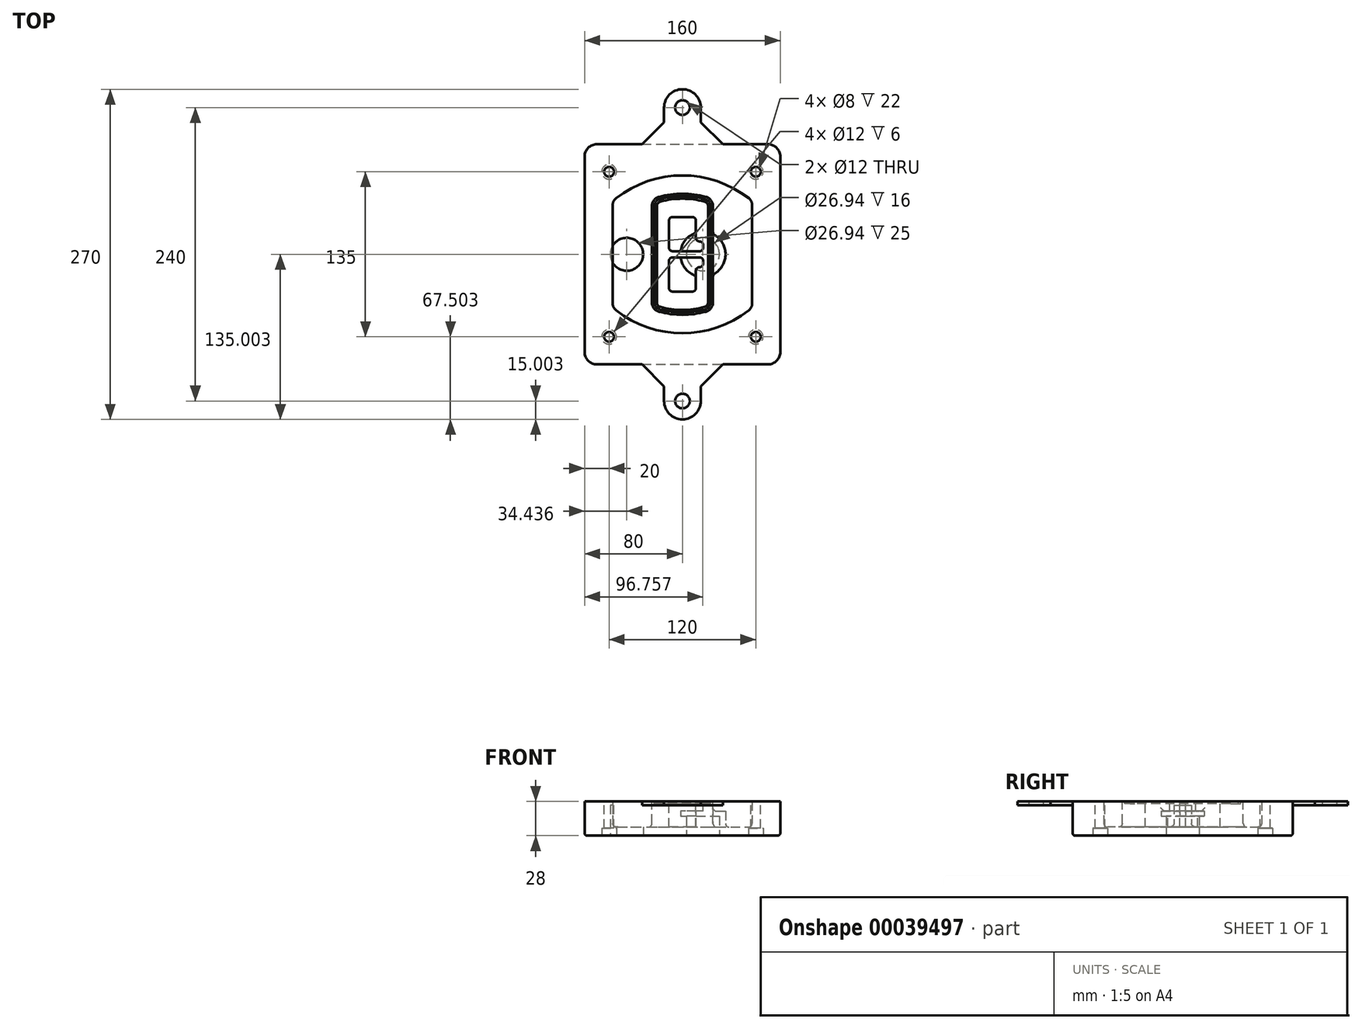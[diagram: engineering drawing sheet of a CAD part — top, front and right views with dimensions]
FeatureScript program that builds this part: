
annotation { "Feature Type Name" : "Feature", "Feature Type Description" : "" }
export const myFeature = defineFeature(function(context is Context, id is Id, definition is map)
    precondition{}
    {
        {
            var Q0;
            Q0=qCreatedBy(makeId("Top.planeOp"),FACE);
            var sketch = newSketch(context, id + "F0", { "sketchPlane" : qUnion([Q0])});
            skPoint(sketch, "E0.rect.middle", {"position": v(0, 0) * mm});
            skLineSegment(sketch, "E1.bottom", {"start": v(24.05, 28.38) * mm, "end": v(164.05, 28.38) * mm});
            skLineSegment(sketch, "E1.top", {"start": v(24.05, 208.38) * mm, "end": v(164.05, 208.38) * mm});
            skLineSegment(sketch, "E1.left", {"start": v(14.05, 38.38) * mm, "end": v(14.05, 198.38) * mm});
            skLineSegment(sketch, "E1.right", {"start": v(174.05, 38.38) * mm, "end": v(174.05, 198.38) * mm});
            skLineSegment(sketch, "E2", {"start": v(14.05, 208.38) * mm, "end": v(174.05, 28.38) * mm, "construction": true});
            skLineSegment(sketch, "E3", {"start": v(174.05, 208.38) * mm, "end": v(14.05, 28.38) * mm, "construction": true});
            skCircle(sketch, "E4", {"center": v(34.05, 185.88) * mm, "radius": 4 * mm});
            skCircle(sketch, "E5", {"center": v(154.05, 185.88) * mm, "radius": 4 * mm});
            skCircle(sketch, "E6", {"center": v(154.05, 50.88) * mm, "radius": 4 * mm});
            skCircle(sketch, "E7", {"center": v(34.05, 50.88) * mm, "radius": 4 * mm});
            skLineSegment(sketch, "E8", {"start": v(34.05, 185.88) * mm, "end": v(154.05, 185.88) * mm, "construction": true});
            skLineSegment(sketch, "E9", {"start": v(154.05, 185.88) * mm, "end": v(154.05, 50.88) * mm, "construction": true});
            skLineSegment(sketch, "E10", {"start": v(154.05, 50.88) * mm, "end": v(34.05, 50.88) * mm, "construction": true});
            skLineSegment(sketch, "E11", {"start": v(34.05, 50.88) * mm, "end": v(34.05, 185.88) * mm, "construction": true});
            skLineSegment(sketch, "E12", {"start": v(34.05, 158.68) * mm, "end": v(34.05, 78.09) * mm});
            skLineSegment(sketch, "E13", {"start": v(154.05, 158.68) * mm, "end": v(154.05, 78.09) * mm});
            skArc(sketch, "E14", {"start": v(150.2, 166.56) * mm, "mid": v(94.05, 185.88) * mm, "end": v(37.9, 166.56) * mm});
            skArc(sketch, "E15", {"start": v(37.9, 70.2) * mm, "mid": v(94.05, 50.88) * mm, "end": v(150.2, 70.2) * mm});
            skLineSegment(sketch, "E16", {"start": v(34.05, 118.38) * mm, "end": v(154.05, 118.38) * mm, "construction": true});
            skPoint(sketch, "E17.visualSharp", {"position": v(34.05, 73.38) * mm});
            skArc(sketch, "E17.filletArc", {"start": v(34.05, 78.09) * mm, "mid": v(35.06, 73.7) * mm, "end": v(37.9, 70.2) * mm});
            skPoint(sketch, "E18.visualSharp", {"position": v(34.05, 163.38) * mm});
            skArc(sketch, "E18.filletArc", {"start": v(37.9, 166.56) * mm, "mid": v(35.06, 163.06) * mm, "end": v(34.05, 158.68) * mm});
            skPoint(sketch, "E19.visualSharp", {"position": v(154.05, 163.38) * mm});
            skArc(sketch, "E19.filletArc", {"start": v(154.05, 158.68) * mm, "mid": v(153.04, 163.06) * mm, "end": v(150.2, 166.56) * mm});
            skPoint(sketch, "E20.visualSharp", {"position": v(154.05, 73.38) * mm});
            skArc(sketch, "E20.filletArc", {"start": v(150.2, 70.2) * mm, "mid": v(153.04, 73.7) * mm, "end": v(154.05, 78.09) * mm});
            skPoint(sketch, "E21.visualSharp", {"position": v(14.05, 208.38) * mm});
            skArc(sketch, "E21.filletArc", {"start": v(24.05, 208.38) * mm, "mid": v(16.98, 205.45) * mm, "end": v(14.05, 198.38) * mm});
            skPoint(sketch, "E22.visualSharp", {"position": v(174.05, 208.38) * mm});
            skArc(sketch, "E22.filletArc", {"start": v(174.05, 198.38) * mm, "mid": v(171.12, 205.45) * mm, "end": v(164.05, 208.38) * mm});
            skPoint(sketch, "E23.visualSharp", {"position": v(174.05, 28.38) * mm});
            skArc(sketch, "E23.filletArc", {"start": v(164.05, 28.38) * mm, "mid": v(171.12, 31.31) * mm, "end": v(174.05, 38.38) * mm});
            skPoint(sketch, "E24.visualSharp", {"position": v(14.05, 28.38) * mm});
            skArc(sketch, "E24.filletArc", {"start": v(14.05, 38.38) * mm, "mid": v(16.98, 31.31) * mm, "end": v(24.05, 28.38) * mm});
            skArc(sketch, "E25.0", {"start": v(151.05, 158.68) * mm, "mid": v(150.34, 161.75) * mm, "end": v(148.36, 164.2) * mm});
            skLineSegment(sketch, "E25.1", {"start": v(151.05, 158.68) * mm, "end": v(151.05, 78.09) * mm});
            skArc(sketch, "E25.2", {"start": v(148.36, 72.57) * mm, "mid": v(150.34, 75.02) * mm, "end": v(151.05, 78.09) * mm});
            skArc(sketch, "E25.3", {"start": v(39.74, 72.57) * mm, "mid": v(94.05, 53.88) * mm, "end": v(148.36, 72.57) * mm});
            skArc(sketch, "E25.4", {"start": v(37.05, 78.09) * mm, "mid": v(37.76, 75.02) * mm, "end": v(39.74, 72.57) * mm});
            skArc(sketch, "E25.5", {"start": v(148.36, 164.2) * mm, "mid": v(94.05, 182.88) * mm, "end": v(39.74, 164.2) * mm});
            skLineSegment(sketch, "E25.6", {"start": v(37.05, 158.68) * mm, "end": v(37.05, 78.09) * mm});
            skArc(sketch, "E25.7", {"start": v(39.74, 164.2) * mm, "mid": v(37.76, 161.75) * mm, "end": v(37.05, 158.68) * mm});
            skArc(sketch, "E26.0", {"start": v(35.43, 169.71) * mm, "mid": v(31.47, 164.82) * mm, "end": v(30.05, 158.68) * mm});
            skArc(sketch, "E26.1", {"start": v(152.67, 169.71) * mm, "mid": v(94.05, 189.88) * mm, "end": v(35.43, 169.71) * mm});
            skArc(sketch, "E26.2", {"start": v(158.05, 158.68) * mm, "mid": v(156.63, 164.82) * mm, "end": v(152.67, 169.71) * mm});
            skLineSegment(sketch, "E26.3", {"start": v(158.05, 158.68) * mm, "end": v(158.05, 78.09) * mm});
            skArc(sketch, "E26.4", {"start": v(152.67, 67.05) * mm, "mid": v(156.63, 71.95) * mm, "end": v(158.05, 78.09) * mm});
            skLineSegment(sketch, "E26.5", {"start": v(30.05, 158.68) * mm, "end": v(30.05, 78.09) * mm});
            skArc(sketch, "E26.6", {"start": v(35.43, 67.05) * mm, "mid": v(94.05, 46.88) * mm, "end": v(152.67, 67.05) * mm});
            skArc(sketch, "E26.7", {"start": v(30.05, 78.09) * mm, "mid": v(31.47, 71.95) * mm, "end": v(35.43, 67.05) * mm});
            skSolve(sketch);
        }
        {
            var Q0;
            Q0=makeQuery(id+"F0.imprint","IMPRINT",FACE,{"disambiguationData":[TD([[makeQuery(id+"F0.imprint","IMPRINT",EDGE,{"derivedFrom":sQuery(id+"F0.wireOp",EDGE,"E1.bottom")}),1.0]])]});
            var Q1;
            Q1=makeQuery(id+"F0.imprint","IMPRINT",FACE,{"disambiguationData":[TD([[makeQuery(id+"F0.imprint","IMPRINT",EDGE,{"derivedFrom":sQuery(id+"F0.wireOp",EDGE,"E12")}),1.0]])]});
            var Q2;
            Q2=makeQuery(id+"F0.imprint","IMPRINT",FACE,{"disambiguationData":[TD([[makeQuery(id+"F0.imprint","IMPRINT",EDGE,{"derivedFrom":sQuery(id+"F0.wireOp",EDGE,"E25.0")}),1.0]])]});
            var Q3;
            Q3=makeQuery(id+"F0.imprint","IMPRINT",FACE,{"disambiguationData":[TD([[makeQuery(id+"F0.imprint","IMPRINT",EDGE,{"derivedFrom":sQuery(id+"F0.wireOp",EDGE,"E12")}),-1.0]])]});
            extrude(context, id + "F1", {"entities" : qUnion([Q0, Q1, Q2, Q3]), "oppositeDirection" : true, "depth" : 25 * mm});
        }
        {
            var Q0;
            Q0=makeQuery(id+"F0.imprint","IMPRINT",FACE,{"disambiguationData":[TD([[makeQuery(id+"F0.imprint","IMPRINT",EDGE,{"derivedFrom":sQuery(id+"F0.wireOp",EDGE,"E12")}),1.0]])]});
            extrude(context, id + "F2", {"entities" : qUnion([Q0]), "operationType" : NewBodyOperationType.ADD, "depth" : 3 * mm});
        }
        {
            var Q0;
            Q0=makeQuery(id+"F0.imprint","IMPRINT",FACE,{"disambiguationData":[TD([[makeQuery(id+"F0.imprint","IMPRINT",EDGE,{"derivedFrom":sQuery(id+"F0.wireOp",EDGE,"E25.0")}),1.0]])]});
            extrude(context, id + "F3", {"entities" : qUnion([Q0]), "operationType" : NewBodyOperationType.REMOVE, "oppositeDirection" : true, "depth" : 18 * mm});
        }
        {
            var Q0;
            Q0=makeQuery(id+"F2.opExtrude","CAP_FACE",FACE,{"disambiguationData":[OSD([sQuery(id+"F0.wireOp",EDGE,"E12"),sQuery(id+"F0.wireOp",EDGE,"E13"),sQuery(id+"F0.wireOp",EDGE,"E14"),sQuery(id+"F0.wireOp",EDGE,"E15"),sQuery(id+"F0.wireOp",EDGE,"E17.filletArc"),sQuery(id+"F0.wireOp",EDGE,"E18.filletArc"),sQuery(id+"F0.wireOp",EDGE,"E19.filletArc"),sQuery(id+"F0.wireOp",EDGE,"E20.filletArc"),sQuery(id+"F0.wireOp",EDGE,"E25.0"),sQuery(id+"F0.wireOp",EDGE,"E25.1"),sQuery(id+"F0.wireOp",EDGE,"E25.2"),sQuery(id+"F0.wireOp",EDGE,"E25.3"),sQuery(id+"F0.wireOp",EDGE,"E25.4"),sQuery(id+"F0.wireOp",EDGE,"E25.5"),sQuery(id+"F0.wireOp",EDGE,"E25.6"),sQuery(id+"F0.wireOp",EDGE,"E25.7")])],"isStart":false});
            var sketch = newSketch(context, id + "F4", { "sketchPlane" : qUnion([Q0])});
            skArc(sketch, "E27.0", {"start": v(74.97, 71.41) * mm, "mid": v(94.05, 68.88) * mm, "end": v(113.13, 71.41) * mm});
            skArc(sketch, "E28.0", {"start": v(113.13, 165.35) * mm, "mid": v(94.05, 167.88) * mm, "end": v(74.97, 165.35) * mm});
            skLineSegment(sketch, "E29", {"start": v(69.05, 157.63) * mm, "end": v(69.05, 79.14) * mm});
            skLineSegment(sketch, "E30", {"start": v(119.05, 157.63) * mm, "end": v(119.05, 79.14) * mm});
            skLineSegment(sketch, "E31", {"start": v(69.05, 163.48) * mm, "end": v(119.05, 163.48) * mm, "construction": true});
            skLineSegment(sketch, "E32", {"start": v(69.05, 73.28) * mm, "end": v(119.05, 73.28) * mm, "construction": true});
            skPoint(sketch, "E33.visualSharp", {"position": v(69.05, 163.48) * mm});
            skArc(sketch, "E33.filletArc", {"start": v(74.97, 165.35) * mm, "mid": v(70.7, 162.5) * mm, "end": v(69.05, 157.63) * mm});
            skPoint(sketch, "E34.visualSharp", {"position": v(119.05, 163.48) * mm});
            skArc(sketch, "E34.filletArc", {"start": v(119.05, 157.63) * mm, "mid": v(117.4, 162.5) * mm, "end": v(113.13, 165.35) * mm});
            skPoint(sketch, "E35.visualSharp", {"position": v(119.05, 73.28) * mm});
            skArc(sketch, "E35.filletArc", {"start": v(113.13, 71.41) * mm, "mid": v(117.4, 74.27) * mm, "end": v(119.05, 79.14) * mm});
            skPoint(sketch, "E36.visualSharp", {"position": v(69.05, 73.28) * mm});
            skArc(sketch, "E36.filletArc", {"start": v(69.05, 79.14) * mm, "mid": v(70.7, 74.27) * mm, "end": v(74.97, 71.41) * mm});
            skArc(sketch, "E37.0", {"start": v(148.36, 164.2) * mm, "mid": v(94.05, 182.88) * mm, "end": v(39.74, 164.2) * mm});
            skArc(sketch, "E37.1", {"start": v(39.74, 164.2) * mm, "mid": v(37.76, 161.75) * mm, "end": v(37.05, 158.68) * mm});
            skLineSegment(sketch, "E37.2", {"start": v(37.05, 158.68) * mm, "end": v(37.05, 78.09) * mm});
            skArc(sketch, "E37.3", {"start": v(37.05, 78.09) * mm, "mid": v(37.76, 75.02) * mm, "end": v(39.74, 72.57) * mm});
            skArc(sketch, "E37.4", {"start": v(39.74, 72.57) * mm, "mid": v(94.05, 53.88) * mm, "end": v(148.36, 72.57) * mm});
            skArc(sketch, "E37.5", {"start": v(148.36, 72.57) * mm, "mid": v(150.34, 75.02) * mm, "end": v(151.05, 78.09) * mm});
            skLineSegment(sketch, "E37.6", {"start": v(151.05, 158.68) * mm, "end": v(151.05, 78.09) * mm});
            skArc(sketch, "E37.7", {"start": v(151.05, 158.68) * mm, "mid": v(150.34, 161.75) * mm, "end": v(148.36, 164.2) * mm});
            skLineSegment(sketch, "E38.0", {"start": v(117.05, 157.63) * mm, "end": v(117.05, 79.14) * mm});
            skArc(sketch, "E38.1", {"start": v(112.61, 73.34) * mm, "mid": v(115.81, 75.49) * mm, "end": v(117.05, 79.14) * mm});
            skArc(sketch, "E38.2", {"start": v(75.49, 73.34) * mm, "mid": v(94.05, 70.88) * mm, "end": v(112.61, 73.34) * mm});
            skArc(sketch, "E38.3", {"start": v(71.05, 79.14) * mm, "mid": v(72.29, 75.49) * mm, "end": v(75.49, 73.34) * mm});
            skLineSegment(sketch, "E38.4", {"start": v(71.05, 157.63) * mm, "end": v(71.05, 79.14) * mm});
            skArc(sketch, "E38.5", {"start": v(117.05, 157.63) * mm, "mid": v(115.81, 161.28) * mm, "end": v(112.61, 163.42) * mm});
            skArc(sketch, "E38.6", {"start": v(75.49, 163.42) * mm, "mid": v(72.29, 161.28) * mm, "end": v(71.05, 157.63) * mm});
            skArc(sketch, "E38.7", {"start": v(112.61, 163.42) * mm, "mid": v(94.05, 165.88) * mm, "end": v(75.49, 163.42) * mm});
            skArc(sketch, "E39.0", {"start": v(115.05, 157.63) * mm, "mid": v(114.23, 160.06) * mm, "end": v(112.1, 161.5) * mm});
            skLineSegment(sketch, "E39.1", {"start": v(115.05, 157.63) * mm, "end": v(115.05, 79.14) * mm});
            skArc(sketch, "E39.2", {"start": v(112.1, 75.27) * mm, "mid": v(114.23, 76.7) * mm, "end": v(115.05, 79.14) * mm});
            skArc(sketch, "E39.3", {"start": v(76, 75.27) * mm, "mid": v(94.05, 72.88) * mm, "end": v(112.1, 75.27) * mm});
            skArc(sketch, "E39.4", {"start": v(73.05, 79.14) * mm, "mid": v(73.87, 76.7) * mm, "end": v(76, 75.27) * mm});
            skArc(sketch, "E39.5", {"start": v(112.1, 161.5) * mm, "mid": v(94.05, 163.88) * mm, "end": v(76, 161.5) * mm});
            skLineSegment(sketch, "E39.6", {"start": v(73.05, 157.63) * mm, "end": v(73.05, 79.14) * mm});
            skArc(sketch, "E39.7", {"start": v(76, 161.5) * mm, "mid": v(73.87, 160.06) * mm, "end": v(73.05, 157.63) * mm});
            skLineSegment(sketch, "E40", {"start": v(69.05, 118.38) * mm, "end": v(119.05, 118.38) * mm, "construction": true});
            skLineSegment(sketch, "E41", {"start": v(83.05, 123.88) * mm, "end": v(83.05, 145.88) * mm});
            skLineSegment(sketch, "E42", {"start": v(86.05, 148.88) * mm, "end": v(102.05, 148.88) * mm});
            skLineSegment(sketch, "E43", {"start": v(105.05, 145.88) * mm, "end": v(105.05, 131.88) * mm});
            skLineSegment(sketch, "E44", {"start": v(108.05, 128.88) * mm, "end": v(108.05, 128.88) * mm});
            skLineSegment(sketch, "E45", {"start": v(111.05, 125.88) * mm, "end": v(111.05, 123.88) * mm});
            skLineSegment(sketch, "E46", {"start": v(108.05, 120.88) * mm, "end": v(86.05, 120.88) * mm});
            skPoint(sketch, "E47.visualSharp", {"position": v(83.05, 148.88) * mm});
            skArc(sketch, "E47.filletArc", {"start": v(86.05, 148.88) * mm, "mid": v(83.93, 148) * mm, "end": v(83.05, 145.88) * mm});
            skPoint(sketch, "E48.visualSharp", {"position": v(105.05, 148.88) * mm});
            skArc(sketch, "E48.filletArc", {"start": v(105.05, 145.88) * mm, "mid": v(104.17, 148) * mm, "end": v(102.05, 148.88) * mm});
            skPoint(sketch, "E49.visualSharp", {"position": v(105.05, 128.88) * mm});
            skArc(sketch, "E49.filletArc", {"start": v(105.05, 131.88) * mm, "mid": v(105.93, 129.76) * mm, "end": v(108.05, 128.88) * mm});
            skPoint(sketch, "E50.visualSharp", {"position": v(111.05, 128.88) * mm});
            skArc(sketch, "E50.filletArc", {"start": v(111.05, 125.88) * mm, "mid": v(110.17, 128) * mm, "end": v(108.05, 128.88) * mm});
            skPoint(sketch, "E51.visualSharp", {"position": v(111.05, 120.88) * mm});
            skArc(sketch, "E51.filletArc", {"start": v(108.05, 120.88) * mm, "mid": v(110.17, 121.76) * mm, "end": v(111.05, 123.88) * mm});
            skPoint(sketch, "E52.visualSharp", {"position": v(83.05, 120.88) * mm});
            skArc(sketch, "E52.filletArc", {"start": v(83.05, 123.88) * mm, "mid": v(83.93, 121.76) * mm, "end": v(86.05, 120.88) * mm});
            skLineSegment(sketch, "E53.0.MirrorCS", {"start": v(108.05, 115.88) * mm, "end": v(86.05, 115.88) * mm});
            skArc(sketch, "E54.0.MirrorCS", {"start": v(83.05, 112.88) * mm, "mid": v(83.93, 115) * mm, "end": v(86.05, 115.88) * mm});
            skLineSegment(sketch, "E55.0.MirrorCS", {"start": v(83.05, 112.88) * mm, "end": v(83.05, 90.88) * mm});
            skArc(sketch, "E56.0.MirrorCS", {"start": v(86.05, 87.88) * mm, "mid": v(83.93, 88.76) * mm, "end": v(83.05, 90.88) * mm});
            skLineSegment(sketch, "E57.0.MirrorCS", {"start": v(86.05, 87.88) * mm, "end": v(102.05, 87.88) * mm});
            skArc(sketch, "E58.0.MirrorCS", {"start": v(105.05, 90.88) * mm, "mid": v(104.17, 88.76) * mm, "end": v(102.05, 87.88) * mm});
            skLineSegment(sketch, "E59.0.MirrorCS", {"start": v(105.05, 90.88) * mm, "end": v(105.05, 104.88) * mm});
            skArc(sketch, "E60.0.MirrorCS", {"start": v(105.05, 104.88) * mm, "mid": v(105.93, 107) * mm, "end": v(108.05, 107.88) * mm});
            skArc(sketch, "E61.0.MirrorCS", {"start": v(111.05, 110.88) * mm, "mid": v(110.17, 108.76) * mm, "end": v(108.05, 107.88) * mm});
            skLineSegment(sketch, "E62.0.MirrorCS", {"start": v(111.05, 110.88) * mm, "end": v(111.05, 112.88) * mm});
            skArc(sketch, "E63.0.MirrorCS", {"start": v(108.05, 115.88) * mm, "mid": v(110.17, 115) * mm, "end": v(111.05, 112.88) * mm});
            skSolve(sketch);
        }
        {
            var Q0;
            Q0=makeQuery(id+"F4.imprint","IMPRINT",FACE,{"disambiguationData":[TD([[makeQuery(id+"F4.imprint","IMPRINT",EDGE,{"derivedFrom":sQuery(id+"F4.wireOp",EDGE,"E27.0")}),1.0]])]});
            var Q1;
            Q1=makeQuery(id+"F4.imprint","IMPRINT",FACE,{"disambiguationData":[TD([[makeQuery(id+"F4.imprint","IMPRINT",EDGE,{"derivedFrom":sQuery(id+"F4.wireOp",EDGE,"E38.0")}),-1.0]])]});
            var Q2;
            Q2=makeQuery(id+"F4.imprint","IMPRINT",FACE,{"disambiguationData":[TD([[makeQuery(id+"F4.imprint","IMPRINT",EDGE,{"derivedFrom":sQuery(id+"F4.wireOp",EDGE,"E39.0")}),1.0]])]});
            extrude(context, id + "F5", {"entities" : qUnion([Q0, Q1, Q2]), "operationType" : NewBodyOperationType.ADD, "endBound" : BoundingType.UP_TO_NEXT, "oppositeDirection" : true, "depth" : 25 * mm});
        }
        {
            var Q0;
            Q0=makeQuery(id+"F4.imprint","IMPRINT",FACE,{"disambiguationData":[TD([[makeQuery(id+"F4.imprint","IMPRINT",EDGE,{"derivedFrom":sQuery(id+"F4.wireOp",EDGE,"E38.0")}),-1.0]])]});
            extrude(context, id + "F6", {"entities" : qUnion([Q0]), "operationType" : NewBodyOperationType.REMOVE, "oppositeDirection" : true, "depth" : 2 * mm});
        }
        {
            var Q0;
            Q0=makeQuery(id+"F1.opExtrude","CAP_FACE",FACE,{"disambiguationData":[OSD([sQuery(id+"F0.wireOp",EDGE,"E1.bottom"),sQuery(id+"F0.wireOp",EDGE,"E1.top"),sQuery(id+"F0.wireOp",EDGE,"E1.left"),sQuery(id+"F0.wireOp",EDGE,"E1.right"),sQuery(id+"F0.wireOp",EDGE,"E4"),sQuery(id+"F0.wireOp",EDGE,"E5"),sQuery(id+"F0.wireOp",EDGE,"E6"),sQuery(id+"F0.wireOp",EDGE,"E7"),sQuery(id+"F0.wireOp",EDGE,"E21.filletArc"),sQuery(id+"F0.wireOp",EDGE,"E22.filletArc"),sQuery(id+"F0.wireOp",EDGE,"E23.filletArc"),sQuery(id+"F0.wireOp",EDGE,"E24.filletArc")])],"isStart":false});
            var sketch = newSketch(context, id + "F7", { "sketchPlane" : qUnion([Q0])});
            skCircle(sketch, "E64", {"center": v(110.8, -118.38) * mm, "radius": 13.47 * mm});
            skCircle(sketch, "E65", {"center": v(48.49, -118.38) * mm, "radius": 13.47 * mm});
            skLineSegment(sketch, "E66", {"start": v(174.05, -118.38) * mm, "end": v(14.05, -118.38) * mm});
            skCircle(sketch, "E67", {"center": v(110.8, -118.38) * mm, "radius": 18.47 * mm});
            skCircle(sketch, "E68", {"center": v(154.05, -185.88) * mm, "radius": 6 * mm});
            skCircle(sketch, "E69", {"center": v(34.05, -185.88) * mm, "radius": 6 * mm});
            skCircle(sketch, "E70", {"center": v(34.05, -50.88) * mm, "radius": 6 * mm});
            skCircle(sketch, "E71", {"center": v(154.05, -50.88) * mm, "radius": 6 * mm});
            skSolve(sketch);
        }
        {
            var Q0;
            {var subQ1=sQuery(id+"F7.wireOp",EDGE,"E66");var subQ4=sQuery(id+"F7.wireOp",EDGE,"E64");var subQ6=makeQuery(id+"F7.imprint","INTERSECT",VERTEX,{"disambiguationData":[OD(0.0)],"derivedFrom":[subQ4,subQ1]});Q0=makeQuery(id+"F7.imprint","IMPRINT",FACE,{"disambiguationData":[TD([[makeQuery(id+"F7.imprint","IMPRINT",EDGE,{"disambiguationData":[TD([[subQ6,-1.0]])],"derivedFrom":subQ4}),-1.0]])]});}
            var Q1;
            {var subQ0=sQuery(id+"F7.wireOp",EDGE,"E66");var subQ1=sQuery(id+"F7.wireOp",EDGE,"E64");var subQ3=makeQuery(id+"F7.imprint","INTERSECT",VERTEX,{"disambiguationData":[OD(0.0)],"derivedFrom":[subQ1,subQ0]});Q1=makeQuery(id+"F7.imprint","IMPRINT",FACE,{"disambiguationData":[TD([[makeQuery(id+"F7.imprint","IMPRINT",EDGE,{"disambiguationData":[TD([[subQ3,-1.0]])],"derivedFrom":subQ1}),1.0]])]});}
            var Q2;
            {var subQ0=sQuery(id+"F7.wireOp",EDGE,"E66");var subQ1=sQuery(id+"F7.wireOp",EDGE,"E64");var subQ3=makeQuery(id+"F7.imprint","INTERSECT",VERTEX,{"disambiguationData":[OD(0.0)],"derivedFrom":[subQ1,subQ0]});Q2=makeQuery(id+"F7.imprint","IMPRINT",FACE,{"disambiguationData":[TD([[makeQuery(id+"F7.imprint","IMPRINT",EDGE,{"disambiguationData":[TD([[subQ3,1.0]])],"derivedFrom":subQ1}),1.0]])]});}
            var Q3;
            {var subQ1=sQuery(id+"F7.wireOp",EDGE,"E66");var subQ4=sQuery(id+"F7.wireOp",EDGE,"E64");var subQ6=makeQuery(id+"F7.imprint","INTERSECT",VERTEX,{"disambiguationData":[OD(0.0)],"derivedFrom":[subQ4,subQ1]});Q3=makeQuery(id+"F7.imprint","IMPRINT",FACE,{"disambiguationData":[TD([[makeQuery(id+"F7.imprint","IMPRINT",EDGE,{"disambiguationData":[TD([[subQ6,1.0]])],"derivedFrom":subQ4}),-1.0]])]});}
            extrude(context, id + "F8", {"entities" : qUnion([Q0, Q1, Q2, Q3]), "operationType" : NewBodyOperationType.ADD, "oppositeDirection" : true, "depth" : 20 * mm});
        }
        {
            var Q0;
            {var subQ0=sQuery(id+"F7.wireOp",EDGE,"E66");var subQ1=sQuery(id+"F7.wireOp",EDGE,"E64");var subQ3=makeQuery(id+"F7.imprint","INTERSECT",VERTEX,{"disambiguationData":[OD(0.0)],"derivedFrom":[subQ1,subQ0]});Q0=makeQuery(id+"F7.imprint","IMPRINT",FACE,{"disambiguationData":[TD([[makeQuery(id+"F7.imprint","IMPRINT",EDGE,{"disambiguationData":[TD([[subQ3,-1.0]])],"derivedFrom":subQ1}),1.0]])]});}
            var Q1;
            {var subQ0=sQuery(id+"F7.wireOp",EDGE,"E66");var subQ1=sQuery(id+"F7.wireOp",EDGE,"E64");var subQ3=makeQuery(id+"F7.imprint","INTERSECT",VERTEX,{"disambiguationData":[OD(0.0)],"derivedFrom":[subQ1,subQ0]});Q1=makeQuery(id+"F7.imprint","IMPRINT",FACE,{"disambiguationData":[TD([[makeQuery(id+"F7.imprint","IMPRINT",EDGE,{"disambiguationData":[TD([[subQ3,1.0]])],"derivedFrom":subQ1}),1.0]])]});}
            extrude(context, id + "F9", {"entities" : qUnion([Q0, Q1]), "operationType" : NewBodyOperationType.REMOVE, "oppositeDirection" : true, "depth" : 16 * mm});
        }
        {
            var Q0;
            {var subQ0=sQuery(id+"F7.wireOp",EDGE,"E66");var subQ1=sQuery(id+"F7.wireOp",EDGE,"E65");var subQ3=makeQuery(id+"F7.imprint","INTERSECT",VERTEX,{"disambiguationData":[OD(0.0)],"derivedFrom":[subQ1,subQ0]});Q0=makeQuery(id+"F7.imprint","IMPRINT",FACE,{"disambiguationData":[TD([[makeQuery(id+"F7.imprint","IMPRINT",EDGE,{"disambiguationData":[TD([[subQ3,-1.0]])],"derivedFrom":subQ1}),1.0]])]});}
            var Q1;
            {var subQ0=sQuery(id+"F7.wireOp",EDGE,"E66");var subQ1=sQuery(id+"F7.wireOp",EDGE,"E65");var subQ3=makeQuery(id+"F7.imprint","INTERSECT",VERTEX,{"disambiguationData":[OD(0.0)],"derivedFrom":[subQ1,subQ0]});Q1=makeQuery(id+"F7.imprint","IMPRINT",FACE,{"disambiguationData":[TD([[makeQuery(id+"F7.imprint","IMPRINT",EDGE,{"disambiguationData":[TD([[subQ3,1.0]])],"derivedFrom":subQ1}),1.0]])]});}
            extrude(context, id + "F10", {"entities" : qUnion([Q0, Q1]), "operationType" : NewBodyOperationType.REMOVE, "oppositeDirection" : true, "depth" : 25 * mm});
        }
        {
            var Q0;
            Q0=makeQuery(id+"F7.imprint","IMPRINT",FACE,{"disambiguationData":[TD([[makeQuery(id+"F7.imprint","IMPRINT",EDGE,{"derivedFrom":sQuery(id+"F7.wireOp",EDGE,"E68")}),1.0]])]});
            var Q1;
            Q1=makeQuery(id+"F7.imprint","IMPRINT",FACE,{"disambiguationData":[TD([[makeQuery(id+"F7.imprint","IMPRINT",EDGE,{"derivedFrom":makeQuery(id+"F1.opExtrude","CAP_EDGE",EDGE,{"disambiguationData":[OSD([sQuery(id+"F0.wireOp",EDGE,"E5")])],"isStart":false})}),-1.0]])]});
            var Q2;
            Q2=makeQuery(id+"F7.imprint","IMPRINT",FACE,{"disambiguationData":[TD([[makeQuery(id+"F7.imprint","IMPRINT",EDGE,{"derivedFrom":sQuery(id+"F7.wireOp",EDGE,"E69")}),1.0]])]});
            var Q3;
            Q3=makeQuery(id+"F7.imprint","IMPRINT",FACE,{"disambiguationData":[TD([[makeQuery(id+"F7.imprint","IMPRINT",EDGE,{"derivedFrom":makeQuery(id+"F1.opExtrude","CAP_EDGE",EDGE,{"disambiguationData":[OSD([sQuery(id+"F0.wireOp",EDGE,"E4")])],"isStart":false})}),-1.0]])]});
            var Q4;
            Q4=makeQuery(id+"F7.imprint","IMPRINT",FACE,{"disambiguationData":[TD([[makeQuery(id+"F7.imprint","IMPRINT",EDGE,{"derivedFrom":sQuery(id+"F7.wireOp",EDGE,"E70")}),1.0]])]});
            var Q5;
            Q5=makeQuery(id+"F7.imprint","IMPRINT",FACE,{"disambiguationData":[TD([[makeQuery(id+"F7.imprint","IMPRINT",EDGE,{"derivedFrom":makeQuery(id+"F1.opExtrude","CAP_EDGE",EDGE,{"disambiguationData":[OSD([sQuery(id+"F0.wireOp",EDGE,"E7")])],"isStart":false})}),-1.0]])]});
            var Q6;
            Q6=makeQuery(id+"F7.imprint","IMPRINT",FACE,{"disambiguationData":[TD([[makeQuery(id+"F7.imprint","IMPRINT",EDGE,{"derivedFrom":sQuery(id+"F7.wireOp",EDGE,"E71")}),1.0]])]});
            var Q7;
            Q7=makeQuery(id+"F7.imprint","IMPRINT",FACE,{"disambiguationData":[TD([[makeQuery(id+"F7.imprint","IMPRINT",EDGE,{"derivedFrom":makeQuery(id+"F1.opExtrude","CAP_EDGE",EDGE,{"disambiguationData":[OSD([sQuery(id+"F0.wireOp",EDGE,"E6")])],"isStart":false})}),-1.0]])]});
            extrude(context, id + "F11", {"entities" : qUnion([Q0, Q1, Q2, Q3, Q4, Q5, Q6, Q7]), "operationType" : NewBodyOperationType.REMOVE, "oppositeDirection" : true, "depth" : 6 * mm});
        }
        {
            var Q0;
            Q0=makeQuery(id+"F9.boolean.opBoolean","COPY",FACE,{"derivedFrom":makeQuery(id+"F9.opExtrude","CAP_FACE",FACE,{"disambiguationData":[OSD([sQuery(id+"F7.wireOp",EDGE,"E64")])],"isStart":false})});
            var sketch = newSketch(context, id + "F12", { "sketchPlane" : qUnion([Q0])});
            skArc(sketch, "E72.0", {"start": v(105.05, -100.83) * mm, "mid": v(96.62, -106.56) * mm, "end": v(92.5, -115.88) * mm});
            skArc(sketch, "E72.1", {"start": v(92.5, -120.88) * mm, "mid": v(96.62, -130.2) * mm, "end": v(105.05, -135.93) * mm});
            skLineSegment(sketch, "E73", {"start": v(92.5, -120.88) * mm, "end": v(108.05, -120.88) * mm});
            skLineSegment(sketch, "E74.0", {"start": v(108.05, -115.88) * mm, "end": v(92.5, -115.88) * mm});
            skArc(sketch, "E74.1", {"start": v(108.05, -115.88) * mm, "mid": v(110.17, -115) * mm, "end": v(111.05, -112.88) * mm});
            skLineSegment(sketch, "E74.2", {"start": v(111.05, -110.88) * mm, "end": v(111.05, -112.88) * mm});
            skArc(sketch, "E74.3", {"start": v(111.05, -110.88) * mm, "mid": v(110.17, -108.76) * mm, "end": v(108.05, -107.88) * mm});
            skArc(sketch, "E74.4", {"start": v(105.05, -104.88) * mm, "mid": v(105.93, -107) * mm, "end": v(108.05, -107.88) * mm});
            skLineSegment(sketch, "E74.5", {"start": v(105.05, -100.83) * mm, "end": v(105.05, -104.88) * mm});
            skLineSegment(sketch, "E74.7", {"start": v(108.05, -120.88) * mm, "end": v(92.5, -120.88) * mm});
            skArc(sketch, "E74.8", {"start": v(108.05, -120.88) * mm, "mid": v(110.17, -121.76) * mm, "end": v(111.05, -123.88) * mm});
            skLineSegment(sketch, "E74.9", {"start": v(111.05, -125.88) * mm, "end": v(111.05, -123.88) * mm});
            skArc(sketch, "E74.10", {"start": v(111.05, -125.88) * mm, "mid": v(110.17, -128) * mm, "end": v(108.05, -128.88) * mm});
            skArc(sketch, "E74.11", {"start": v(105.05, -131.88) * mm, "mid": v(105.93, -129.76) * mm, "end": v(108.05, -128.88) * mm});
            skLineSegment(sketch, "E74.12", {"start": v(105.05, -135.93) * mm, "end": v(105.05, -131.88) * mm});
            skPoint(sketch, "E75.orphan", {"position": v(105.05, -145.88) * mm});
            skPoint(sketch, "E76.orphan", {"position": v(86.05, -120.88) * mm});
            skPoint(sketch, "E77.orphan", {"position": v(86.05, -115.88) * mm});
            skPoint(sketch, "E78.orphan", {"position": v(105.05, -90.88) * mm});
            skSolve(sketch);
        }
        {
            var Q0;
            {var subQ7=sQuery(id+"F12.wireOp",EDGE,"E72.0");var subQ14=sQuery(id+"F12.wireOp",EDGE,"E72.1");var subQ16=sQuery(id+"F12.wireOp",EDGE,"E74.1");var subQ18=sQuery(id+"F12.wireOp",EDGE,"E74.8");Q0=qUnion([makeQuery(id+"F12.imprint","IMPRINT",FACE,{"disambiguationData":[TD([[makeQuery(id+"F12.imprint","IMPRINT",EDGE,{"derivedFrom":subQ7}),1.0]])]}),makeQuery(id+"F12.imprint","IMPRINT",FACE,{"disambiguationData":[TD([[makeQuery(id+"F12.imprint","IMPRINT",EDGE,{"derivedFrom":subQ14}),1.0]])]}),makeQuery(id+"F12.imprint","IMPRINT",FACE,{"disambiguationData":[TD([[makeQuery(id+"F12.imprint","IMPRINT",EDGE,{"derivedFrom":subQ16}),1.0]])]}),makeQuery(id+"F12.imprint","IMPRINT",FACE,{"disambiguationData":[TD([[makeQuery(id+"F12.imprint","IMPRINT",EDGE,{"derivedFrom":subQ18}),-1.0]])]})]);}
            var Q1;
            Q1=makeQuery(id+"F5.boolean.opBoolean","SPLIT",FACE,{"disambiguationData":[TD([makeQuery(id+"F5.opExtrude","SWEPT_FACE",FACE,{"disambiguationData":[OSD([sQuery(id+"F4.wireOp",EDGE,"E41")])]})])],"derivedFrom":makeQuery(id+"F3.boolean.opBoolean","COPY",FACE,{"derivedFrom":makeQuery(id+"F3.opExtrude","CAP_FACE",FACE,{"disambiguationData":[OSD([sQuery(id+"F0.wireOp",EDGE,"E25.0"),sQuery(id+"F0.wireOp",EDGE,"E25.1"),sQuery(id+"F0.wireOp",EDGE,"E25.2"),sQuery(id+"F0.wireOp",EDGE,"E25.3"),sQuery(id+"F0.wireOp",EDGE,"E25.4"),sQuery(id+"F0.wireOp",EDGE,"E25.5"),sQuery(id+"F0.wireOp",EDGE,"E25.6"),sQuery(id+"F0.wireOp",EDGE,"E25.7")])],"isStart":false})})});
            extrude(context, id + "F13", {"entities" : qUnion([Q0]), "operationType" : NewBodyOperationType.REMOVE, "endBound" : BoundingType.UP_TO_SURFACE, "endBoundEntityFace" : qUnion([Q1]), "depth" : 25 * mm});
        }
        {
            var Q0;
            Q0=makeQuery(id+"F3.boolean.opBoolean","COPY",EDGE,{"derivedFrom":makeQuery(id+"F3.opExtrude","CAP_EDGE",EDGE,{"disambiguationData":[OSD([sQuery(id+"F0.wireOp",EDGE,"E25.6")])],"isStart":false})});
            var Q1;
            Q1=makeQuery(id+"F8.boolean.opBoolean","INTERSECT",EDGE,{"derivedFrom":[makeQuery(id+"F5.opExtrude","SWEPT_FACE",FACE,{"disambiguationData":[OSD([sQuery(id+"F4.wireOp",EDGE,"E30")])]}),makeQuery(id+"F8.opExtrude","CAP_FACE",FACE,{"disambiguationData":[OSD([sQuery(id+"F7.wireOp",EDGE,"E67")])],"isStart":false})]});
            var Q2;
            Q2=makeQuery(id+"F8.boolean.opBoolean","INTERSECT",EDGE,{"disambiguationData":[OD(1.0)],"derivedFrom":[makeQuery(id+"F5.opExtrude","SWEPT_FACE",FACE,{"disambiguationData":[OSD([sQuery(id+"F4.wireOp",EDGE,"E30")])]}),makeQuery(id+"F8.opExtrude","SWEPT_FACE",FACE,{"disambiguationData":[OSD([sQuery(id+"F7.wireOp",EDGE,"E67")])]})]});
            var Q3;
            {var subQ0=sQuery(id+"F4.wireOp",EDGE,"E30");Q3=makeQuery(id+"F8.boolean.opBoolean","SPLIT",EDGE,{"disambiguationData":[TD([makeQuery(id+"F5.opExtrude","SWEPT_FACE",FACE,{"disambiguationData":[OSD([sQuery(id+"F4.wireOp",EDGE,"E35.filletArc")])]})])],"derivedFrom":makeQuery(id+"F5.opExtrude","CAP_EDGE",EDGE,{"disambiguationData":[OSD([subQ0])],"isStart":false})});}
            var Q4;
            {var subQ0=sQuery(id+"F0.wireOp",EDGE,"E25.7");var subQ1=sQuery(id+"F0.wireOp",EDGE,"E25.1");var subQ2=sQuery(id+"F0.wireOp",EDGE,"E25.6");var subQ3=sQuery(id+"F0.wireOp",EDGE,"E25.5");var subQ4=sQuery(id+"F0.wireOp",EDGE,"E25.4");var subQ5=sQuery(id+"F0.wireOp",EDGE,"E25.0");var subQ6=sQuery(id+"F0.wireOp",EDGE,"E25.2");var subQ7=sQuery(id+"F0.wireOp",EDGE,"E25.3");Q4=makeQuery(id+"F8.boolean.opBoolean","INTERSECT",EDGE,{"derivedFrom":[makeQuery(id+"F5.boolean.opBoolean","SPLIT",FACE,{"disambiguationData":[TD([makeQuery(id+"F2.opExtrude","SWEPT_FACE",FACE,{"disambiguationData":[OSD([subQ5])]})])],"derivedFrom":makeQuery(id+"F3.boolean.opBoolean","COPY",FACE,{"derivedFrom":makeQuery(id+"F3.opExtrude","CAP_FACE",FACE,{"disambiguationData":[OSD([subQ5,subQ1,subQ6,subQ7,subQ4,subQ3,subQ2,subQ0])],"isStart":false})})}),makeQuery(id+"F8.opExtrude","SWEPT_FACE",FACE,{"disambiguationData":[OSD([sQuery(id+"F7.wireOp",EDGE,"E67")])]})]});}
            var Q5;
            Q5=makeQuery(id+"F8.boolean.opBoolean","INTERSECT",EDGE,{"disambiguationData":[OD(0.0)],"derivedFrom":[makeQuery(id+"F5.opExtrude","SWEPT_FACE",FACE,{"disambiguationData":[OSD([sQuery(id+"F4.wireOp",EDGE,"E30")])]}),makeQuery(id+"F8.opExtrude","SWEPT_FACE",FACE,{"disambiguationData":[OSD([sQuery(id+"F7.wireOp",EDGE,"E67")])]})]});
            fillet(context, id + "F14", {"entities" : qUnion([Q0, Q1, Q2, Q3, Q4, Q5]), "radius" : 3 * mm, "tangentPropagation" : true, "allowEdgeOverflow" : false});
        }
        {
            var Q0;
            Q0=makeQuery(id+"F1.opExtrude","CAP_EDGE",EDGE,{"disambiguationData":[OSD([sQuery(id+"F0.wireOp",EDGE,"E1.bottom")])],"isStart":false});
            fillet(context, id + "F15", {"entities" : qUnion([Q0]), "radius" : 2 * mm, "tangentPropagation" : true, "allowEdgeOverflow" : false});
        }
        {
            var Q0;
            {var subQ0=sQuery(id+"F0.wireOp",EDGE,"E1.bottom");var subQ1=sQuery(id+"F0.wireOp",EDGE,"E1.top");var subQ2=sQuery(id+"F0.wireOp",EDGE,"E1.left");var subQ3=sQuery(id+"F0.wireOp",EDGE,"E1.right");var subQ4=sQuery(id+"F0.wireOp",EDGE,"E4");var subQ5=sQuery(id+"F0.wireOp",EDGE,"E5");var subQ6=sQuery(id+"F0.wireOp",EDGE,"E6");var subQ7=sQuery(id+"F0.wireOp",EDGE,"E7");var subQ8=sQuery(id+"F0.wireOp",EDGE,"E21.filletArc");var subQ9=sQuery(id+"F0.wireOp",EDGE,"E22.filletArc");var subQ10=sQuery(id+"F0.wireOp",EDGE,"E23.filletArc");var subQ11=sQuery(id+"F0.wireOp",EDGE,"E24.filletArc");Q0=makeQuery(id+"F2.boolean.opBoolean","SPLIT",FACE,{"disambiguationData":[TD([makeQuery(id+"F1.opExtrude","SWEPT_FACE",FACE,{"disambiguationData":[OSD([subQ0])]})])],"derivedFrom":makeQuery(id+"F1.opExtrude","CAP_FACE",FACE,{"disambiguationData":[OSD([subQ0,subQ1,subQ2,subQ3,subQ4,subQ5,subQ6,subQ7,subQ8,subQ9,subQ10,subQ11])],"isStart":true})});}
            var sketch = newSketch(context, id + "F16", { "sketchPlane" : qUnion([Q0])});
            skArc(sketch, "E79.0", {"start": v(37.9, 166.56) * mm, "mid": v(35.06, 163.06) * mm, "end": v(34.05, 158.68) * mm});
            skArc(sketch, "E79.1", {"start": v(150.2, 166.56) * mm, "mid": v(94.05, 185.88) * mm, "end": v(37.9, 166.56) * mm});
            skLineSegment(sketch, "E79.2", {"start": v(34.05, 158.68) * mm, "end": v(34.05, 78.09) * mm});
            skArc(sketch, "E79.3", {"start": v(34.05, 78.09) * mm, "mid": v(35.06, 73.7) * mm, "end": v(37.9, 70.2) * mm});
            skArc(sketch, "E79.4", {"start": v(37.9, 70.2) * mm, "mid": v(94.05, 50.88) * mm, "end": v(150.2, 70.2) * mm});
            skArc(sketch, "E79.5", {"start": v(150.2, 70.2) * mm, "mid": v(153.04, 73.7) * mm, "end": v(154.05, 78.09) * mm});
            skLineSegment(sketch, "E79.6", {"start": v(154.05, 158.68) * mm, "end": v(154.05, 78.09) * mm});
            skArc(sketch, "E79.7", {"start": v(154.05, 158.68) * mm, "mid": v(153.04, 163.06) * mm, "end": v(150.2, 166.56) * mm});
            skCircle(sketch, "E79.8", {"center": v(154.05, 185.88) * mm, "radius": 4 * mm});
            skArc(sketch, "E79.9", {"start": v(174.05, 198.38) * mm, "mid": v(171.12, 205.45) * mm, "end": v(164.05, 208.38) * mm});
            skLineSegment(sketch, "E79.10", {"start": v(24.05, 208.38) * mm, "end": v(164.05, 208.38) * mm});
            skLineSegment(sketch, "E79.11", {"start": v(174.05, 38.38) * mm, "end": v(174.05, 198.38) * mm});
            skArc(sketch, "E79.12", {"start": v(24.05, 208.38) * mm, "mid": v(16.98, 205.45) * mm, "end": v(14.05, 198.38) * mm});
            skLineSegment(sketch, "E79.13", {"start": v(14.05, 38.38) * mm, "end": v(14.05, 198.38) * mm});
            skArc(sketch, "E79.14", {"start": v(14.05, 38.38) * mm, "mid": v(16.98, 31.31) * mm, "end": v(24.05, 28.38) * mm});
            skLineSegment(sketch, "E79.15", {"start": v(24.05, 28.38) * mm, "end": v(164.05, 28.38) * mm});
            skCircle(sketch, "E79.16", {"center": v(34.05, 50.88) * mm, "radius": 4 * mm});
            skCircle(sketch, "E79.17", {"center": v(154.05, 50.88) * mm, "radius": 4 * mm});
            skArc(sketch, "E79.18", {"start": v(164.05, 28.38) * mm, "mid": v(171.12, 31.31) * mm, "end": v(174.05, 38.38) * mm});
            skLineSegment(sketch, "E80", {"start": v(94.05, 208.38) * mm, "end": v(94.05, 238.38) * mm, "construction": true});
            skCircle(sketch, "E81", {"center": v(94.05, 238.38) * mm, "radius": 6 * mm});
            skLineSegment(sketch, "E82", {"start": v(79.05, 238.38) * mm, "end": v(79.05, 226.38) * mm});
            skLineSegment(sketch, "E83", {"start": v(109.05, 238.38) * mm, "end": v(109.05, 226.38) * mm});
            skLineSegment(sketch, "E84", {"start": v(109.05, 226.38) * mm, "end": v(127.05, 208.38) * mm});
            skArc(sketch, "E85", {"start": v(109.05, 238.38) * mm, "mid": v(94.05, 253.38) * mm, "end": v(79.05, 238.38) * mm});
            skLineSegment(sketch, "E86.MirrorCS", {"start": v(79.05, 226.38) * mm, "end": v(61.05, 208.38) * mm});
            skArc(sketch, "E87.MirrorCS", {"start": v(79.05, 238.38) * mm, "mid": v(94.05, 253.38) * mm, "end": v(109.05, 238.38) * mm});
            skLineSegment(sketch, "E88", {"start": v(14.05, 118.38) * mm, "end": v(174.05, 118.38) * mm, "construction": true});
            skLineSegment(sketch, "E89.MirrorCS", {"start": v(79.05, 10.38) * mm, "end": v(61.05, 28.38) * mm});
            skLineSegment(sketch, "E90.MirrorCS", {"start": v(79.05, -1.62) * mm, "end": v(79.05, 10.38) * mm});
            skArc(sketch, "E91.MirrorCS", {"start": v(109.05, -1.62) * mm, "mid": v(94.05, -16.62) * mm, "end": v(79.05, -1.62) * mm});
            skLineSegment(sketch, "E92.MirrorCS", {"start": v(109.05, -1.62) * mm, "end": v(109.05, 10.38) * mm});
            skLineSegment(sketch, "E93.MirrorCS", {"start": v(109.05, 10.38) * mm, "end": v(127.05, 28.38) * mm});
            skLineSegment(sketch, "E94.MirrorCS", {"start": v(94.05, 28.38) * mm, "end": v(94.05, -1.62) * mm});
            skCircle(sketch, "E95.MirrorC", {"center": v(94.05, -1.62) * mm, "radius": 6 * mm});
            skSolve(sketch);
        }
        {
            var Q0;
            Q0=makeQuery(id+"F16.imprint","IMPRINT",FACE,{"disambiguationData":[TD([[makeQuery(id+"F16.imprint","IMPRINT",EDGE,{"derivedFrom":sQuery(id+"F16.wireOp",EDGE,"E81")}),-1.0]])]});
            var Q1;
            Q1=makeQuery(id+"F16.imprint","IMPRINT",FACE,{"disambiguationData":[TD([[makeQuery(id+"F16.imprint","IMPRINT",EDGE,{"derivedFrom":sQuery(id+"F16.wireOp",EDGE,"E79.0")}),-1.0]])]});
            var Q2;
            {var subQ3=sQuery(id+"F16.wireOp",EDGE,"E89.MirrorCS");Q2=makeQuery(id+"F16.imprint","IMPRINT",FACE,{"disambiguationData":[TD([[makeQuery(id+"F16.imprint","IMPRINT",EDGE,{"derivedFrom":subQ3}),-1.0]])]});}
            var Q3;
            {var subQ0=sQuery(id+"F4.wireOp",EDGE,"E36.filletArc");var subQ1=sQuery(id+"F4.wireOp",EDGE,"E35.filletArc");var subQ2=sQuery(id+"F4.wireOp",EDGE,"E34.filletArc");var subQ3=sQuery(id+"F4.wireOp",EDGE,"E33.filletArc");var subQ4=sQuery(id+"F4.wireOp",EDGE,"E27.0");var subQ5=sQuery(id+"F4.wireOp",EDGE,"E30");var subQ6=sQuery(id+"F4.wireOp",EDGE,"E28.0");var subQ7=sQuery(id+"F4.wireOp",EDGE,"E29");Q3=makeQuery(id+"F6.boolean.opBoolean","SPLIT",FACE,{"disambiguationData":[TD([makeQuery(id+"F5.opExtrude","SWEPT_FACE",FACE,{"disambiguationData":[OSD([subQ4])]})])],"derivedFrom":makeQuery(id+"F5.opExtrude","CAP_FACE",FACE,{"disambiguationData":[OSD([subQ4,subQ6,subQ7,subQ5,subQ3,subQ2,subQ1,subQ0,sQuery(id+"F4.wireOp",EDGE,"E41"),sQuery(id+"F4.wireOp",EDGE,"E42"),sQuery(id+"F4.wireOp",EDGE,"E43"),sQuery(id+"F4.wireOp",EDGE,"E45"),sQuery(id+"F4.wireOp",EDGE,"E46"),sQuery(id+"F4.wireOp",EDGE,"E47.filletArc"),sQuery(id+"F4.wireOp",EDGE,"E48.filletArc"),sQuery(id+"F4.wireOp",EDGE,"E49.filletArc"),sQuery(id+"F4.wireOp",EDGE,"E50.filletArc"),sQuery(id+"F4.wireOp",EDGE,"E51.filletArc"),sQuery(id+"F4.wireOp",EDGE,"E52.filletArc"),sQuery(id+"F4.wireOp",EDGE,"E53.0.MirrorCS"),sQuery(id+"F4.wireOp",EDGE,"E54.0.MirrorCS"),sQuery(id+"F4.wireOp",EDGE,"E55.0.MirrorCS"),sQuery(id+"F4.wireOp",EDGE,"E56.0.MirrorCS"),sQuery(id+"F4.wireOp",EDGE,"E57.0.MirrorCS"),sQuery(id+"F4.wireOp",EDGE,"E58.0.MirrorCS"),sQuery(id+"F4.wireOp",EDGE,"E59.0.MirrorCS"),sQuery(id+"F4.wireOp",EDGE,"E60.0.MirrorCS"),sQuery(id+"F4.wireOp",EDGE,"E61.0.MirrorCS"),sQuery(id+"F4.wireOp",EDGE,"E62.0.MirrorCS"),sQuery(id+"F4.wireOp",EDGE,"E63.0.MirrorCS")])],"isStart":true})});}
            extrude(context, id + "F17", {"entities" : qUnion([Q0, Q1, Q2]), "operationType" : NewBodyOperationType.ADD, "endBound" : BoundingType.UP_TO_SURFACE, "endBoundEntityFace" : qUnion([Q3]), "depth" : 25 * mm});
        }
    });
